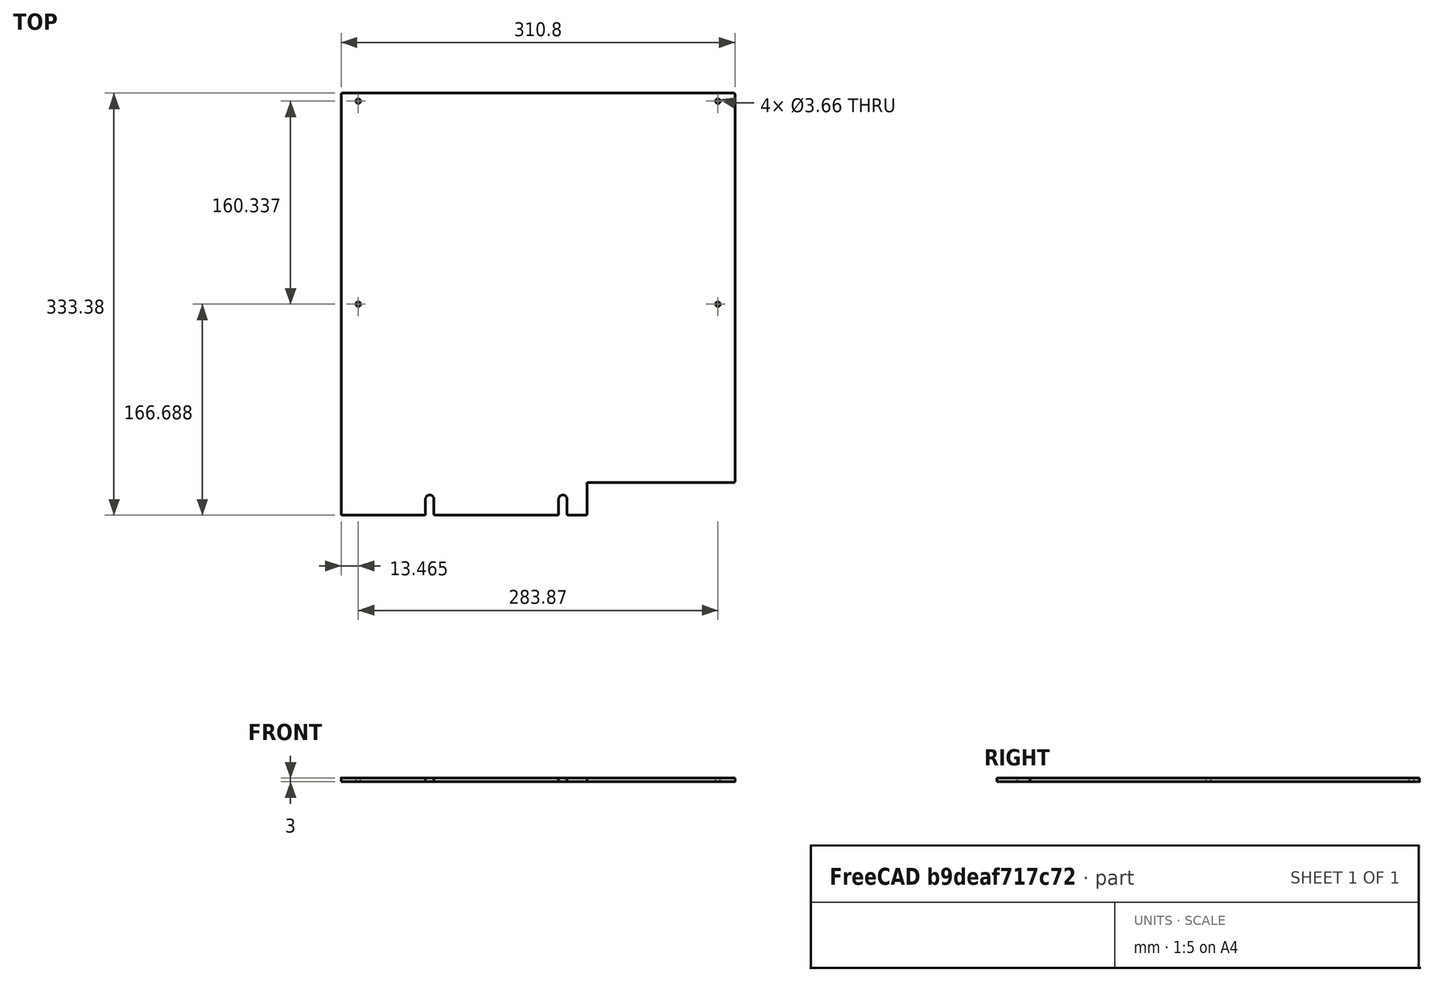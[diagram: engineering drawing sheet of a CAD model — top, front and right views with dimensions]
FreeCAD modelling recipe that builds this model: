
FCSTD DOCUMENT  (FreeCAD 0.21R33675 (Git))
Label: sleep_box_side
License: All rights reserved
LicenseURL: http://en.wikipedia.org/wiki/All_rights_reserved
objects: Sketcher::SketchObject×1, Spreadsheet::Sheet×1, PartDesign::Pad×1, PartDesign::Body×1
note: 4 computed .brp shape members not serialized (recipe doc carries the construction recipe); baked Part::Feature solids carry a one-line shape summary decoded from their .brp

FEATURE [Sketcher::SketchObject] Sketch
  FullyConstrained = true
  MapMode = 5
  Support = -> [XY_Plane]
  expr: Constraints[11] = Spreadsheet.FilletRadius
  expr: Constraints[12] = Spreadsheet.Length
  expr: Constraints[21] = Spreadsheet.MountHoleDistanceFromBottom
  expr: Constraints[24] = Spreadsheet.MountHoleDiameter
  expr: Constraints[28] = Spreadsheet.MountHoleSideMargin1
  expr: Constraints[41] = Spreadsheet.Height
  expr: Constraints[46] = Spreadsheet.DoorCutOutLengthWithMargin
  expr: Constraints[47] = Spreadsheet.DoorCutoutHeightWithMargin
  expr: Constraints[54] = Spreadsheet.MountHoleSideMargin2
  expr: Constraints[62] = Spreadsheet.BracketHoleFromSide
  expr: Constraints[63] = Spreadsheet.UpperBracketHoleFromTop
  expr: Constraints[67] = Spreadsheet.BracketHoleDiameter
  expr: Constraints[74] = Spreadsheet.BracketHoleFromSide
  expr: Constraints[75] = Spreadsheet.UpperBracketHoleFromTop
  sketch-geometry (46):
    g0: ArcOfCircle CenterX=-154.4 CenterY=332.375 CenterZ=0 NormalX=0 NormalY=0 NormalZ=1 AngleXU=0 Radius=1 StartAngle=1.5708 EndAngle=3.14159
    g1: LineSegment StartX=-154.4 StartY=333.375 StartZ=0 EndX=154.4 EndY=333.375 EndZ=0
    g2: ArcOfCircle CenterX=154.4 CenterY=332.375 CenterZ=0 NormalX=0 NormalY=0 NormalZ=1 AngleXU=0 Radius=1 StartAngle=-8.9e-15 EndAngle=1.5708
    g3: LineSegment StartX=155.4 StartY=332.375 StartZ=0 EndX=155.4 EndY=26.9 EndZ=0
    g4: ArcOfCircle CenterX=-154.4 CenterY=1 CenterZ=0 NormalX=0 NormalY=0 NormalZ=1 AngleXU=0 Radius=1 StartAngle=3.14159 EndAngle=4.71239
    g5: LineSegment StartX=-155.4 StartY=1 StartZ=0 EndX=-155.4 EndY=332.375 EndZ=0
    g6: GeomPoint X=-155.4 Y=333.375 Z=0
    g7: LineSegment StartX=-85.55 StartY=12.7 StartZ=0 EndX=-155.4 EndY=12.7 EndZ=0
    g8: LineSegment StartX=19.55 StartY=12.7 StartZ=0 EndX=38.6 EndY=12.7 EndZ=0
    g9: Circle CenterX=-85.55 CenterY=12.7 CenterZ=0 NormalX=0 NormalY=0 NormalZ=1 AngleXU=0 Radius=3.302
    g10: Circle CenterX=19.55 CenterY=12.7 CenterZ=0 NormalX=0 NormalY=0 NormalZ=1 AngleXU=0 Radius=3.302
    g11: LineSegment StartX=0 StartY=12.7 StartZ=0 EndX=0 EndY=0 EndZ=0
    g12: LineSegment StartX=-85.55 StartY=12.7 StartZ=0 EndX=0 EndY=12.7 EndZ=0
    g13: LineSegment StartX=0 StartY=12.7 StartZ=0 EndX=19.55 EndY=12.7 EndZ=0
    g14: LineSegment StartX=38.6 StartY=1 StartZ=0 EndX=38.6 EndY=24.9 EndZ=0
    g15: LineSegment StartX=39.6 StartY=25.9 StartZ=0 EndX=154.4 EndY=25.9 EndZ=0
    g16: LineSegment StartX=-154.4 StartY=0 StartZ=0 EndX=37.6 EndY=0 EndZ=0
    g17: ArcOfCircle CenterX=37.6 CenterY=1 CenterZ=0 NormalX=0 NormalY=0 NormalZ=1 AngleXU=0 Radius=1 StartAngle=4.71239 EndAngle=6.28319
    g18: ArcOfCircle CenterX=39.6 CenterY=24.9 CenterZ=0 NormalX=0 NormalY=0 NormalZ=1 AngleXU=0 Radius=1 StartAngle=1.5708 EndAngle=3.14159
    g19: ArcOfCircle CenterX=154.4 CenterY=26.9 CenterZ=0 NormalX=0 NormalY=0 NormalZ=1 AngleXU=0 Radius=1 StartAngle=4.71239 EndAngle=6.28319
    g20: LineSegment StartX=38.6 StartY=12.7 StartZ=0 EndX=155.4 EndY=12.7 EndZ=0
    g21: LineSegment StartX=155.4 StartY=26.9 StartZ=0 EndX=155.4 EndY=12.7 EndZ=0
    g22: LineSegment StartX=-141.935 StartY=333.375 StartZ=0 EndX=-141.935 EndY=327.025 EndZ=0
    g23: LineSegment StartX=-141.935 StartY=327.025 StartZ=0 EndX=-141.935 EndY=166.687 EndZ=0
    g24: LineSegment StartX=-141.935 StartY=166.687 StartZ=0 EndX=-155.4 EndY=166.687 EndZ=0
    g25: Circle CenterX=-141.935 CenterY=327.025 CenterZ=0 NormalX=0 NormalY=0 NormalZ=1 AngleXU=0 Radius=1.8288
    g26: Circle CenterX=-141.935 CenterY=166.687 CenterZ=0 NormalX=0 NormalY=0 NormalZ=1 AngleXU=0 Radius=1.8288
    g27: LineSegment StartX=141.935 StartY=333.375 StartZ=0 EndX=141.935 EndY=327.025 EndZ=0
    g28: LineSegment StartX=141.935 StartY=327.025 StartZ=0 EndX=141.935 EndY=166.687 EndZ=0
    g29: LineSegment StartX=141.935 StartY=166.687 StartZ=0 EndX=155.4 EndY=166.687 EndZ=0
    g30: Circle CenterX=141.935 CenterY=327.025 CenterZ=0 NormalX=0 NormalY=0 NormalZ=1 AngleXU=0 Radius=1.8288
    g31: Circle CenterX=141.935 CenterY=166.687 CenterZ=0 NormalX=0 NormalY=0 NormalZ=1 AngleXU=0 Radius=1.8288
    g32: LineSegment StartX=141.935 StartY=166.687 StartZ=0 EndX=-141.935 EndY=166.687 EndZ=0
    g33: ArcOfCircle CenterX=-85.55 CenterY=12.7 CenterZ=0 NormalX=0 NormalY=0 NormalZ=1 AngleXU=0 Radius=3.302 StartAngle=0 EndAngle=3.14159
    g34: LineSegment StartX=-88.852 StartY=12.7 StartZ=0 EndX=-88.852 EndY=1 EndZ=0
    g35: LineSegment StartX=-82.248 StartY=12.7 StartZ=0 EndX=-82.248 EndY=1 EndZ=0
    g36: ArcOfCircle CenterX=-89.852 CenterY=1 CenterZ=0 NormalX=0 NormalY=0 NormalZ=1 AngleXU=0 Radius=1 StartAngle=4.71239 EndAngle=6.28319
    g37: ArcOfCircle CenterX=-81.248 CenterY=1 CenterZ=0 NormalX=0 NormalY=0 NormalZ=1 AngleXU=0 Radius=1 StartAngle=3.14159 EndAngle=4.71239
    g38: ArcOfCircle CenterX=19.55 CenterY=12.7 CenterZ=0 NormalX=0 NormalY=0 NormalZ=1 AngleXU=0 Radius=3.302 StartAngle=0 EndAngle=3.14159
    g39: LineSegment StartX=16.248 StartY=12.7 StartZ=0 EndX=16.248 EndY=1 EndZ=0
    g40: LineSegment StartX=22.852 StartY=12.7 StartZ=0 EndX=22.852 EndY=1 EndZ=0
    g41: ArcOfCircle CenterX=15.248 CenterY=1 CenterZ=0 NormalX=0 NormalY=0 NormalZ=1 AngleXU=0 Radius=1 StartAngle=4.71239 EndAngle=6.28319
    g42: ArcOfCircle CenterX=23.852 CenterY=1 CenterZ=0 NormalX=0 NormalY=0 NormalZ=1 AngleXU=0 Radius=1 StartAngle=3.14159 EndAngle=4.71239
    g43: LineSegment StartX=-154.4 StartY=0 StartZ=0 EndX=-89.852 EndY=0 EndZ=0
    g44: LineSegment StartX=-81.248 StartY=0 StartZ=0 EndX=15.248 EndY=0 EndZ=0
    g45: LineSegment StartX=23.852 StartY=0 StartZ=0 EndX=37.6 EndY=0 EndZ=0
  constraints (118):
    c: Tangent(g0,g1) = 1.5708
    c: Tangent(g1,g2) = 1.5708
    c: Tangent(g2,g3) = 1.5708
    c: Tangent(g4,g5) = 1.5708
    c: Tangent(g5,g0) = 1.5708
    c: Horizontal(g1)
    c: Vertical(g3)
    c: Vertical(g5)
    c: Equal(g0,g2)
    c: PointOnObject(g6,g1)
    c: PointOnObject(g6,g5)
    c: Radius(g2) = 1
    c: DistanceX(g0,g2) = 310.8
    c: PointOnObject(g7,g5)
    c: Horizontal(g7)
    c: Horizontal(g8)
    c: Vertical(g11)
    c: Coincident(g12,g9)
    c: Horizontal(g12)
    c: Coincident(g13,g10)
    c: Horizontal(g13)
    c: DistanceY(g11,g11) = 12.7
    c: Coincident(g7,g9)
    c: Coincident(g10,g8)
    c: Diameter(g10) = 6.604
    c: Coincident(g13,g11)
    c: Coincident(g12,g11)
    c: Equal(g9,g10)
    c: DistanceX(g8,g8) = 19.05
    c: Vertical(g14)
    c: Horizontal(g15)
    c: PointOnObject(g8,g14)
    c: Horizontal(g16)
    c: Tangent(g16,g4) = -1.5708
    c: PointOnObject(g11,g16)
    c: Tangent(g14,g17) = -1.5708
    c: Tangent(g16,g17) = -1.5708
    c: Tangent(g14,g18) = 1.5708
    c: Tangent(g15,g18) = 1.5708
    c: Tangent(g15,g19) = -1.5708
    c: Tangent(g3,g19) = 1.5708
    c: DistanceY(g4,g6) = 333.375
    c: Equal(g4,g0)
    c: Equal(g4,g17)
    c: Equal(g17,g18)
    c: Equal(g18,g19)
    c: DistanceX(g14,g3) = 116.8
    c: DistanceY(g16,g15) = 25.9
    c: Coincident(g20,g8)
    c: Coincident(g21,g3)
    c: Vertical(g21)
    c: Coincident(g20,g21)
    c: Symmetric(g7,g20,g11)
    c: Coincident(g11,g-1)
    c: DistanceX(g7,g9) = 69.85
    c: PointOnObject(g22,g1)
    c: Vertical(g22)
    c: Coincident(g22,g23)
    c: Vertical(g23)
    c: Coincident(g23,g24)
    c: Horizontal(g24)
    c: Symmetric(g0,g4,g24)
    c: DistanceX(g6,g22) = 13.4648
    c: DistanceY(g22,g22) = 6.35
    c: Coincident(g25,g22)
    c: Coincident(g26,g23)
    c: Equal(g26,g25)
    c: Diameter(g25) = 3.6576
    c: PointOnObject(g27,g1)
    c: Vertical(g27)
    c: Coincident(g27,g28)
    c: Vertical(g28)
    c: Coincident(g28,g29)
    c: Horizontal(g29)
    c: DistanceX(g27,g2) = 13.4648
    c: DistanceY(g27,g27) = 6.35
    c: Coincident(g30,g27)
    c: Coincident(g31,g28)
    c: Equal(g31,g30)
    c: Equal(g30,g25)
    c: PointOnObject(g29,g3)
    c: Coincident(g32,g31)
    c: Horizontal(g32)
    c: Coincident(g32,g26)
    c: Coincident(g33,g7)
    c: PointOnObject(g33,g7)
    c: PointOnObject(g33,g12)
    c: PointOnObject(g33,g9)
    c: Coincident(g34,g33)
    c: Vertical(g34)
    c: Coincident(g35,g33)
    c: Vertical(g35)
    c: Equal(g34,g35)
    c: Tangent(g36,g34) = 1.5708
    c: Tangent(g36,g16) = -1.5708
    c: Tangent(g37,g35) = -1.5708
    c: Tangent(g37,g16) = -1.5708
    c: Equal(g36,g4)
    c: Coincident(g38,g8)
    c: PointOnObject(g38,g13)
    c: PointOnObject(g38,g8)
    c: Tangent(g38,g10) = -1.5708
    c: Coincident(g39,g38)
    c: Vertical(g39)
    c: Coincident(g40,g38)
    c: Vertical(g40)
    c: Equal(g39,g40)
    c: Tangent(g41,g39) = 1.5708
    c: Tangent(g41,g16) = -1.5708
    c: Tangent(g42,g40) = -1.5708
    c: Tangent(g42,g16) = -1.5708
    c: Equal(g42,g17)
    c: Coincident(g43,g4)
    c: Coincident(g43,g36)
    c: Coincident(g44,g37)
    c: Coincident(g44,g41)
    c: Coincident(g45,g42)
    c: Coincident(g45,g17)
FEATURE [Spreadsheet::Sheet] Spreadsheet
  cells = A2='Parameters; A3='BeamHeight; B3(BeamHeight)==1 in; A4='FloorHeight; B4(FloorHeight)==BeamHeight + 0.125 in; A5='HeightAboveFloor; B5(HeightAboveFloor)==12 in; A6='Height; B6(Height)==HeightAboveFloor + FloorHeight; A7='Length; B7(Length)==310.8 mm; A8='Thickness; B8(Thickness)==3 mm; A9='FilletRadius; B9(FilletRadius)==1 mm; A10='MountHoleDiameter; B10(MountHoleDiameter)==0.26 in; A11='MountHoleDistanceFromBottom; B11(MountHoleDistanceFromBottom)==0.5 in; A12='MountHoleSideMargin1; B12(MountHoleSideMargin1)==0.75 in; A13='MountHoleSideMargin2; B13(MountHoleSideMargin2)==2.75 in; A14='WallMargin; B14(WallMargin)==0.5 mm; A15='DoorCutoutLength; B15(DoorCutoutLength)==116.3 mm; A16='DoorCutOutLengthWithMargin; B16(DoorCutOutLengthWithMargin)==DoorCutoutLength + WallMargin; A17='DoorCutoutHeight; B17(DoorCutoutHeight)==BeamHeight; A18='DoorCutoutHeightWithMargin; B18(DoorCutoutHeightWithMargin)==DoorCutoutHeight + WallMargin; A20='BracketWidth; B20(BracketWidth)==0.5 in; A21='BracketHoleDiameter; B21(BracketHoleDiameter)==0.144 in; A22='BracketHoleOffset; B22(BracketHoleOffset)==0.412 in; A23='UpperBracketHoleFromTop; B23(UpperBracketHoleFromTop)==0.5 * BracketWidth; A24='BracketHoleFromSide; B24(BracketHoleFromSide)==BracketHoleOffset + Thickness
FEATURE [PartDesign::Pad] Pad
  Direction = (0,0,1)
  Length = 3
  Length2 = 10
  Profile = -> Sketch
  ReferenceAxis = -> Sketch [N_Axis]
  Type = 0
  expr: Length = Spreadsheet.Thickness
FEATURE [PartDesign::Body] Body
  Group = -> [Sketch,Pad]
  Origin = -> Origin
  Tip = -> Pad
